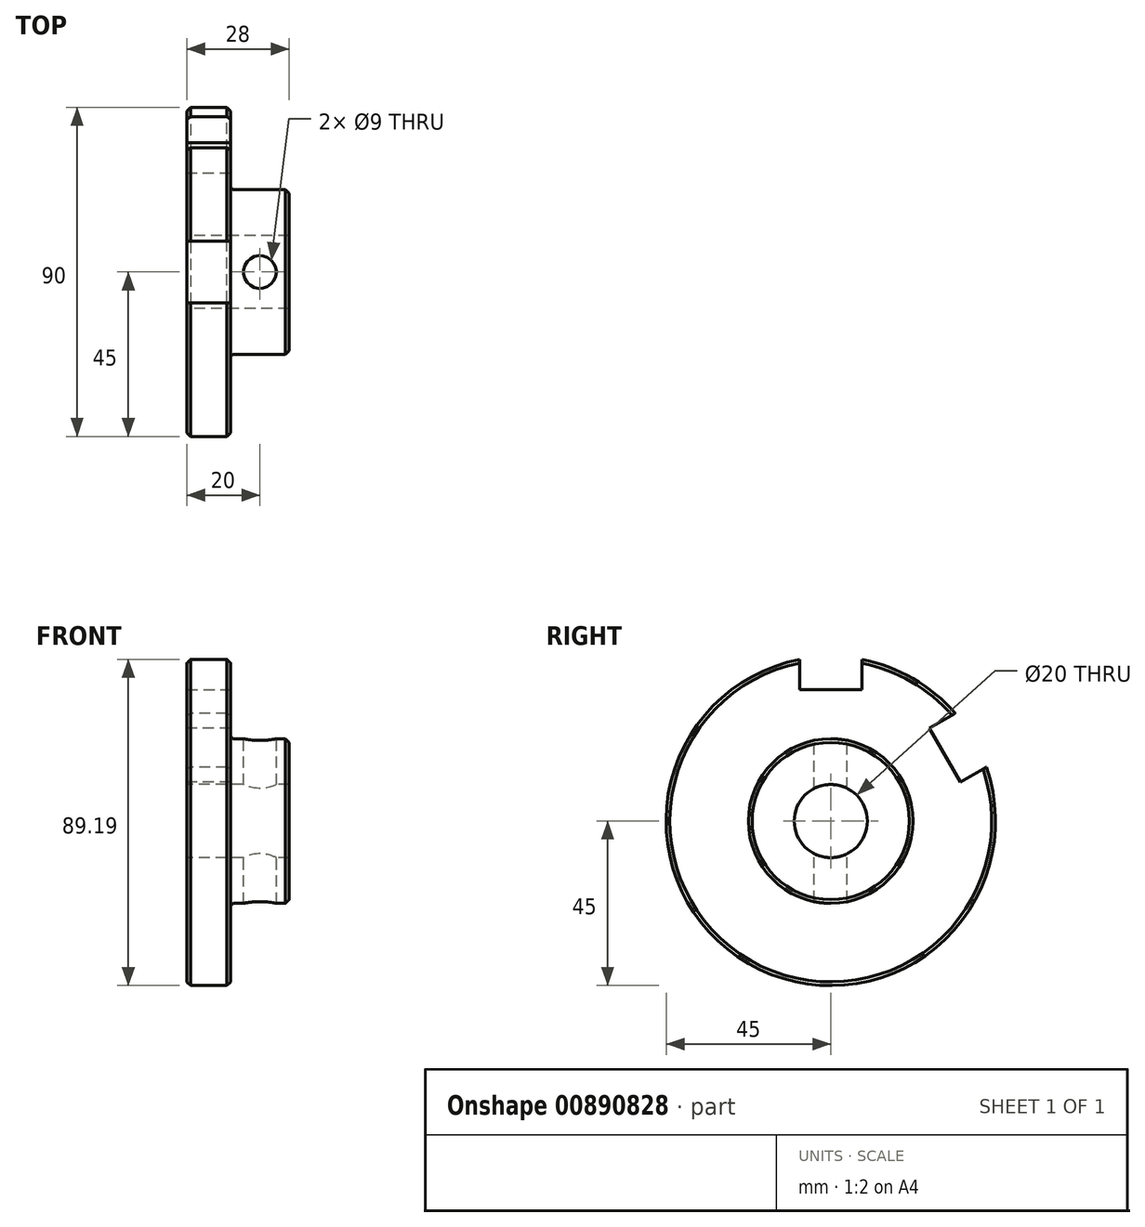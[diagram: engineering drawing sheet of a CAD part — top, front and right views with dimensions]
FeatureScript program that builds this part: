
annotation { "Feature Type Name" : "Feature", "Feature Type Description" : "" }
export const myFeature = defineFeature(function(context is Context, id is Id, definition is map)
    precondition{}
    {
        {
            var Q0;
            Q0=qCreatedBy(makeId("Front.planeOp"),FACE);
            var sketch = newSketch(context, id + "F0", { "sketchPlane" : qUnion([Q0])});
            skLineSegment(sketch, "E0", {"start": v(0, 10) * mm, "end": v(0, 45) * mm});
            skLineSegment(sketch, "E1", {"start": v(0, 45) * mm, "end": v(12, 45) * mm});
            skLineSegment(sketch, "E2", {"start": v(12, 45) * mm, "end": v(12, 22.5) * mm});
            skLineSegment(sketch, "E3", {"start": v(12, 22.5) * mm, "end": v(28, 22.5) * mm});
            skLineSegment(sketch, "E4", {"start": v(28, 22.5) * mm, "end": v(28, 10) * mm});
            skLineSegment(sketch, "E5", {"start": v(28, 10) * mm, "end": v(0, 10) * mm});
            skSolve(sketch);
        }
        {
            var Q0;
            Q0=qCreatedBy(makeId("Front.planeOp"),FACE);
            var sketch = newSketch(context, id + "F1", { "sketchPlane" : qUnion([Q0])});
            skLineSegment(sketch, "E6", {"start": v(-16.18, 0) * mm, "end": v(52.32, 0) * mm});
            skSolve(sketch);
        }
        {
            var Q0;
            Q0=makeQuery(id+"F0.imprint","IMPRINT",FACE,{"disambiguationData":[TD([[makeQuery(id+"F0.imprint","IMPRINT",EDGE,{"derivedFrom":sQuery(id+"F0.wireOp",EDGE,"E0")}),-1.0]])]});
            var Q1;
            Q1=sQuery(id+"F1.wireOp",EDGE,"E6");
            revolve(context, id + "F2", {"surfaceOperationType" : NewSurfaceOperationType.NEW, "entities" : qUnion([Q0]), "axis" : qUnion([Q1]), "revolveType" : RevolveType.FULL});
        }
        {
            var Q0;
            Q0=qCreatedBy(makeId("Top.planeOp"),FACE);
            var sketch = newSketch(context, id + "F3", { "sketchPlane" : qUnion([Q0])});
            skCircle(sketch, "E7", {"center": v(20, 0) * mm, "radius": 4.5 * mm});
            skSolve(sketch);
        }
        {
            var Q0;
            Q0=makeQuery(id+"F3.imprint","IMPRINT",FACE,{"disambiguationData":[TD([[makeQuery(id+"F3.imprint","IMPRINT",EDGE,{"derivedFrom":sQuery(id+"F3.wireOp",EDGE,"E7")}),1.0]])]});
            extrude(context, id + "F4", {"entities" : qUnion([Q0]), "operationType" : NewBodyOperationType.REMOVE, "endBound" : BoundingType.SYMMETRIC, "oppositeDirection" : true, "depth" : 50 * mm, "offsetDistance" : 25 * mm});
        }
        {
            var Q0;
            Q0=makeQuery(id+"F2.opRevolve","SWEPT_FACE",FACE,{"disambiguationData":[OSD([sQuery(id+"F0.wireOp",EDGE,"E2")])]});
            var sketch = newSketch(context, id + "F5", { "sketchPlane" : qUnion([Q0])});
            skLineSegment(sketch, "E8", {"start": v(-8.5, 50) * mm, "end": v(-8.5, 36) * mm});
            skLineSegment(sketch, "E9", {"start": v(-8.5, 36) * mm, "end": v(8.5, 36) * mm});
            skLineSegment(sketch, "E10", {"start": v(8.5, 36) * mm, "end": v(8.5, 50) * mm});
            skLineSegment(sketch, "E11", {"start": v(8.5, 50) * mm, "end": v(-8.5, 50) * mm});
            skSolve(sketch);
        }
        {
            var Q0;
            Q0 = qSketchRegion(id + "F5", true);
            extrude(context, id + "F6", {"entities" : qUnion([Q0]), "operationType" : NewBodyOperationType.REMOVE, "oppositeDirection" : true, "depth" : 25 * mm, "offsetDistance" : 25 * mm});
        }
        {
            var Q0;
            Q0=qCreatedBy(makeId("Right.planeOp"),FACE);
            var sketch = newSketch(context, id + "F7", { "sketchPlane" : qUnion([Q0])});
            skLineSegment(sketch, "E12", {"start": v(0, 0) * mm, "end": v(55.4, 31.98) * mm});
            skLineSegment(sketch, "E13", {"start": v(36.28, 30.76) * mm, "end": v(26.93, 25.36) * mm});
            skLineSegment(sketch, "E14", {"start": v(26.93, 25.36) * mm, "end": v(35.43, 10.64) * mm});
            skLineSegment(sketch, "E15", {"start": v(35.43, 10.64) * mm, "end": v(44.78, 16.04) * mm});
            skLineSegment(sketch, "E16", {"start": v(44.78, 16.04) * mm, "end": v(36.28, 30.76) * mm});
            skLineSegment(sketch, "E17", {"start": v(-29.2, 50.59) * mm, "end": v(0, 0) * mm});
            skSolve(sketch);
        }
        {
            var Q0;
            Q0 = qSketchRegion(id + "F7", true);
            extrude(context, id + "F8", {"entities" : qUnion([Q0]), "operationType" : NewBodyOperationType.REMOVE, "depth" : 25 * mm, "offsetDistance" : 25 * mm});
        }
        {
            var Q0;
            Q0=makeQuery(id+"F2.opRevolve","SWEPT_EDGE",EDGE,{"disambiguationData":[OSD([sQuery(id+"F0.wireOp",EDGE,"E3"),sQuery(id+"F0.wireOp",EDGE,"E4")])]});
            var Q1;
            {var subQ0=sQuery(id+"F0.wireOp",EDGE,"E1");var subQ1=sQuery(id+"F0.wireOp",EDGE,"E2");Q1=makeQuery(id+"F8.boolean.opBoolean","SPLIT",EDGE,{"disambiguationData":[TD([makeQuery(id+"F6.boolean.opBoolean","COPY",FACE,{"derivedFrom":makeQuery(id+"F6.opExtrude","SWEPT_FACE",FACE,{"disambiguationData":[OSD([sQuery(id+"F5.wireOp",EDGE,"E10")])]})})])],"derivedFrom":makeQuery(id+"F2.opRevolve","SWEPT_EDGE",EDGE,{"disambiguationData":[OSD([subQ0,subQ1])]})});}
            var Q2;
            {var subQ0=sQuery(id+"F0.wireOp",EDGE,"E0");var subQ1=sQuery(id+"F0.wireOp",EDGE,"E1");Q2=makeQuery(id+"F8.boolean.opBoolean","SPLIT",EDGE,{"disambiguationData":[TD([makeQuery(id+"F6.boolean.opBoolean","COPY",FACE,{"derivedFrom":makeQuery(id+"F6.opExtrude","SWEPT_FACE",FACE,{"disambiguationData":[OSD([sQuery(id+"F5.wireOp",EDGE,"E10")])]})})])],"derivedFrom":makeQuery(id+"F2.opRevolve","SWEPT_EDGE",EDGE,{"disambiguationData":[OSD([subQ0,subQ1])]})});}
            var Q3;
            {var subQ0=sQuery(id+"F0.wireOp",EDGE,"E0");var subQ1=sQuery(id+"F0.wireOp",EDGE,"E1");Q3=makeQuery(id+"F8.boolean.opBoolean","SPLIT",EDGE,{"disambiguationData":[TD([makeQuery(id+"F6.boolean.opBoolean","COPY",FACE,{"derivedFrom":makeQuery(id+"F6.opExtrude","SWEPT_FACE",FACE,{"disambiguationData":[OSD([sQuery(id+"F5.wireOp",EDGE,"E8")])]})})])],"derivedFrom":makeQuery(id+"F2.opRevolve","SWEPT_EDGE",EDGE,{"disambiguationData":[OSD([subQ0,subQ1])]})});}
            var Q4;
            {var subQ0=sQuery(id+"F0.wireOp",EDGE,"E1");var subQ1=sQuery(id+"F0.wireOp",EDGE,"E2");Q4=makeQuery(id+"F8.boolean.opBoolean","SPLIT",EDGE,{"disambiguationData":[TD([makeQuery(id+"F6.boolean.opBoolean","COPY",FACE,{"derivedFrom":makeQuery(id+"F6.opExtrude","SWEPT_FACE",FACE,{"disambiguationData":[OSD([sQuery(id+"F5.wireOp",EDGE,"E8")])]})})])],"derivedFrom":makeQuery(id+"F2.opRevolve","SWEPT_EDGE",EDGE,{"disambiguationData":[OSD([subQ0,subQ1])]})});}
            chamfer(context, id + "F9", {"entities" : qUnion([Q0, Q1, Q2, Q3, Q4]), "width" : 1 * mm, "tangentPropagation" : true});
        }
        {
            var Q0;
            Q0=makeQuery(id+"F2.opRevolve","SWEPT_EDGE",EDGE,{"disambiguationData":[OSD([sQuery(id+"F0.wireOp",EDGE,"E2"),sQuery(id+"F0.wireOp",EDGE,"E3")])]});
            fillet(context, id + "F10", {"entities" : qUnion([Q0]), "tangentPropagation" : true, "radius" : 1 * mm, "defaultsChanged" : true, "vertexSettings" : [], "allowEdgeOverflow" : false});
        }
    });
